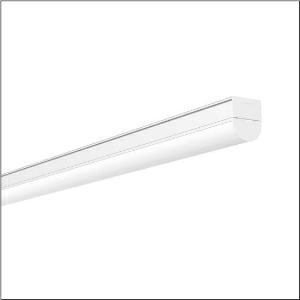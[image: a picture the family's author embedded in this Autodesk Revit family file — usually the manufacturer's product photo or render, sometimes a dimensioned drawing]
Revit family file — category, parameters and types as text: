
# Revit family: ecopack_r__31_51lj12mdm20a_29c1
name_source: partatom
category: Lighting Fixtures
units: mm (PartAtom-declared; Revit-internal decimal feet)

## family parameters
Cut with Voids When Loaded = No
Host = Face
Light Source = No
Part Type = Normal
Room Calculation Point = No
Round Connector Dimension = Use Diameter
Shared = No

## types (1)
- --- (1 x LED, 2510 lm, 20 W, 5000K)
    Apparent Load = 20 VA
    CIE Flux Codes = 41 71 90 93 100
    Color Rendering = 80
    Color Temperature = 5000K
    Default Elevation = 1800 mm
    Description = Ecopack® 31, diffuser luminaire, primary optical cover: cover, of PC, frosted, light emission: direct distribution, primary light characteristic: symmetric, installation type: surface-mounted, LED, rated luminous flux: 2.600lm, luminous efficacy: 130lm/W, light colour: 830/840/850, colour temperature: 3000/4000/5000K, control gear: ECG, with terminal, 3-pole, mains connection: 220..240V, AC, 50/60Hz, rated input power: 20W, housing, of aluminium, traffic white (RAL 9016), length: 600mm, width: 56mm, height: 68mm, end cap, of PC, white, protection rating (complete): IP20, insulation class (complete): insulation class I (protective earthing), certification: CE, impact resistance: IK06, permissible operating ambient temperature: -20..+40°C, packaging unit: 1 piece
    Height = 68 mm
    Lamp = 1 x LED
    Lamp Light Flux = 2510 lm
    Lamp Power = 20 W
    Lamp count = 1
    Length = 600 mm
    Luminous efficacy = 126 lm/W
    Manufacturer = Siteco
    ModVariant = No
    Model = 51LJ12MDM20A
    Mounting Place = Ceiling
    Mounting Type = Surface mounted
    Number of Poles = 1
    OnlyDefault = Yes
    Power Factor = 1
    Product Name = Ecopack® 31
    Product group = diffuser luminaire
    ProductGroupID = 305
    Protection Class = Protection class I
    Protection Degree = IP 20
    RLX_Detail_Level = 1
    RLX_Emergency_Light_Flux = 0 lm
    RLX_Emergency_Type = 0
    RLX_Emergency_Type_DB = No
    RlxData = <blob elided: 25581 chars, md5=ab6cc6c8>
    Socket = socket
    Standby Power = 0 W
    System Light Flux = 2510 lm
    System Power = 20 W
    Type Comments = individual setting: colour temperature 5000K, luminous flux: 100 % | (ON | ON)
    Type Image = l_1007030.jpg
    URL = http://relux.com
    VarID = @adj_145165
    Voltage = 0 V
    Weight = 0.00 kg
    Width = 56 mm

## geometry (parser evidence)
native form markers: Blend x4, Sweep x13
no freeform markers — native parametric forms only
